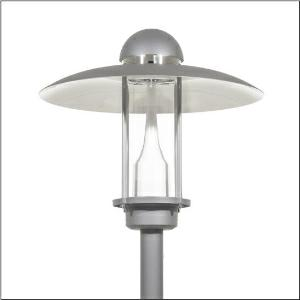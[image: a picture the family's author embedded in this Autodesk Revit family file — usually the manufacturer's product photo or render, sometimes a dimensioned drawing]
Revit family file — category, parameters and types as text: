
# Revit family: city-light_elegance_iq___p1_0a_5xa5265lf14h_79ad
name_source: partatom
category: Lighting Fixtures
units: mm (PartAtom-declared; Revit-internal decimal feet)

## family parameters
Cut with Voids When Loaded = No
Host = Face
Light Source = No
Part Type = Normal
Room Calculation Point = No
Round Connector Dimension = Use Diameter
Shared = No

## types (1)
- --- (1 x LED, 1440 lm, 10 W, 4000K)
    Apparent Load = 10 VA
    CIE Flux Codes = 32 62 91 97 100
    Color Rendering = 70
    Color Temperature = 4000K
    Default Elevation = 1800 mm
    Description = City-Light Elegance iQ, mast luminaire, Module 540 iQ-SR, primary light control with 3 zone facetted reflector, of plastic, silver coated, highly specular, structured, primary optical cover: cover, of PMMA, transparent, light distribution: P1.0a, light emission: direct distribution, primary light characteristic: strongly asymmetric, installation type: post-top, LED, High Power LED, rated luminous flux: 1.440lm, luminous efficacy: 144lm/W, light colour: 740, colour temperature: 4000K, control gear: ECG iQ, control: presetting dimming logarithmic, Street-Remote, Auto-Match, Temp-Guard, Lumen-Switch, Night-Set, Smart-Wire, Light-Fading, Desk-Remote (wireless, voltage-free reading and setting of iQ features in the workshop via application-optimized NFC function/RFID function), optimised constant luminous flux control (CLO 2.0), with terminal, 6-pole, max. 2.5mm², mains connection: 230..240V, AC, 50/60Hz, start of lifetime: 10W, end of service life: 10W, reduction: 5W, luminaire housing, upper part, of aluminium, coated, Siteco® metallic grey (DB 702S), diameter: 750mm, height: 675mm, spigot size: d x l = 76 x 70mm (post-top) | with reducer (optional accessory) 60 x 70mm, post-top mast mounting element, of diecast aluminium, coated, Siteco® metallic grey (DB 702S), Module 540 iQ-SR, traffic white (RAL 9016), equipment: standard, protection rating (complete): IP65, insulation class (complete): insulation class II (safety insulation), certification: CE, ENEC, VDE, packaging unit: 1 piece

Light Distribution: P1.0a
    Height = 675 mm
    Lamp = 1 x LED
    Lamp Light Flux = 1440 lm
    Lamp Power = 10 W
    Lamp count = 1
    Length = 750 mm
    Luminous efficacy = 144 lm/W
    Manufacturer = Siteco
    ModVariant = No
    Model = 5XA5265LF14H
    Number of Poles = 1
    OnlyDefault = Yes
    Power Factor = 1
    Product Name = City-Light Elegance iQ | P1.0a
    Product group = mast luminaire | pylon top
    ProductGroupID = 6100
    Protection Class = Protection class II
    Protection Degree = IP 65
    RLX_Detail_Level = 1
    RLX_Emergency_Light_Flux = 0 lm
    RLX_Emergency_Type = 0
    RLX_Emergency_Type_DB = No
    RlxData = <blob elided: 106209 chars, md5=6c80fdf8>
    Socket = socket
    Standby Power = 0 W
    System Light Flux = 1440 lm
    System Power = 10 W
    Type Comments = factory setting: luminous flux: 100 % | dim-lin: 254 | 401 mA
    Type Image = l_1006912.jpg
    URL = http://relux.com
    VarID = @adj_109869
    Voltage = 0 V
    Weight = 0.00 kg
    Width = 0 mm  [stored 0 ft]

note: [stored X ft] marks values corroborated as IEEE doubles in the binary element streams (Revit-internal decimal feet)

## geometry (parser evidence)
native form markers: Blend x4, Sweep x11
no freeform markers — native parametric forms only
